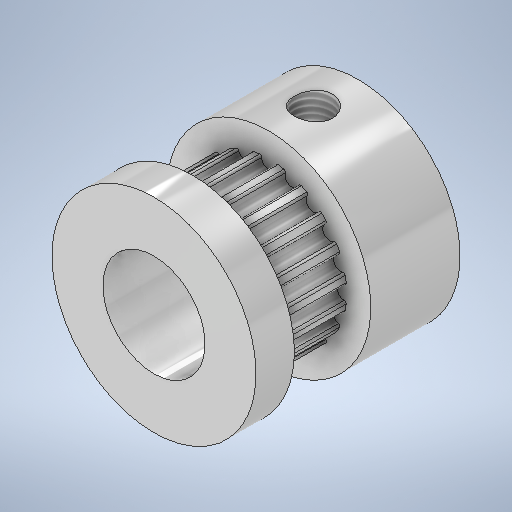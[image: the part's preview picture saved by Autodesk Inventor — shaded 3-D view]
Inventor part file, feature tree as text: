
AUTODESK INVENTOR PART (.ipt)
format: ipt  version: 2025.2 (Build 292293000, 293)  size: 384,512 bytes
history: native  units: mm
features: sketch x3, extrude x2, other x1, revolve x1, pattern_circular x1, plane x1, thread x1
ambient origin geometry x8: Origin, YZ Plane, XZ Plane, XY Plane, X Axis, Y Axis, Z Axis, Center Point
bodies: Body1 (feature_tree)
feature tree (10):
  other  "Sólido1"
  revolve  "Revolución1"  [1 undecoded]
  extrude  "Extrusión1"  Depth=6.0mm
  pattern_circular  "Patrón circular1"  [2 undecoded]
  plane  "Plano de trabajo1"
  extrude  "Extrusión2"  TaperAngle=360.0deg  [1 undecoded]
  thread  "Rosca1"  [1 undecoded]
  sketch  "Boceto1"  dims[d0=16.0mm d1=7.0mm]
  sketch  "Boceto2"  dims[d2=10.724mm d3=6.0mm]
  sketch  "Boceto3"  dims[d5=16.0mm d7=4.0mm d8=360.0deg d9=1.570796mm d10=3.141593mm d25=0.555mm d26=0.555mm d27=0.75mm d28=1.11mm d29=0.628319mm d31=0.555mm d32=0.15mm d33=6.112mm d34=10.0mm d35=0.0mm d36=200.0mm d37=360.0deg d39=3.0mm d40=3.5mm d41=0.0mm d42=0.0mm d43=109.917mm d44=0.0mm]
note: 5 required parameter values undecoded (feature->parameter linkage not recoverable at this tier; creation-order binding heuristic only, values carry confidence <= 0.55)